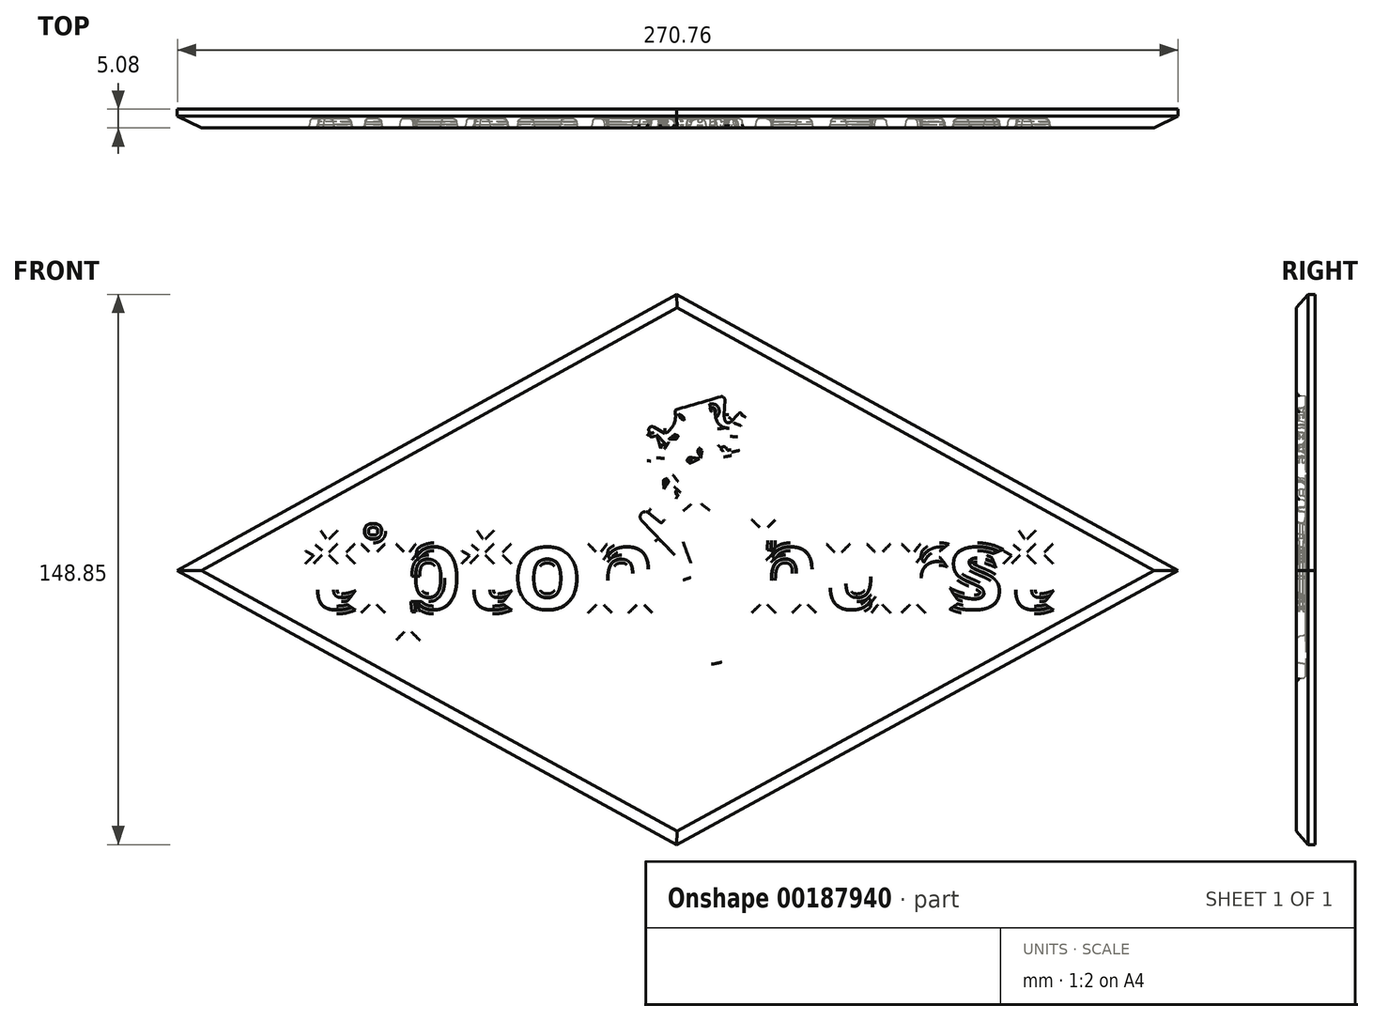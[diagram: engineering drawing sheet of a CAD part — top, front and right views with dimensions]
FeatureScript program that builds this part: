
annotation { "Feature Type Name" : "Feature", "Feature Type Description" : "" }
export const myFeature = defineFeature(function(context is Context, id is Id, definition is map)
    precondition{}
    {
        {
            var Q0;
            Q0=qCreatedBy(makeId("Front.planeOp"),FACE);
            var sketch = newSketch(context, id + "F0", { "sketchPlane" : qUnion([Q0])});
            skLineSegment(sketch, "E0", {"start": v(-28.06, 100.3) * mm, "end": v(-163.18, 25.63) * mm});
            skLineSegment(sketch, "E1", {"start": v(-163.18, 25.63) * mm, "end": v(-28.06, -48.54) * mm});
            skLineSegment(sketch, "E2", {"start": v(-28.06, -48.54) * mm, "end": v(107.58, 25.63) * mm});
            skLineSegment(sketch, "E3", {"start": v(107.58, 25.63) * mm, "end": v(-28.06, 100.3) * mm});
            skSolve(sketch);
        }
        {
            var Q0;
            Q0=makeQuery(id+"F0.imprint","IMPRINT",FACE,{"disambiguationData":[TD([[makeQuery(id+"F0.imprint","IMPRINT",EDGE,{"derivedFrom":sQuery(id+"F0.wireOp",EDGE,"E0")}),1.0]])]});
            extrude(context, id + "F1", {"entities" : qUnion([Q0]), "depth" : 5.08 * mm});
        }
        {
            var Q0;
            Q0=makeQuery(id+"F1.opExtrude","CAP_FACE",FACE,{"disambiguationData":[OSD([sQuery(id+"F0.wireOp",EDGE,"E0"),sQuery(id+"F0.wireOp",EDGE,"E1"),sQuery(id+"F0.wireOp",EDGE,"E2"),sQuery(id+"F0.wireOp",EDGE,"E3")])],"isStart":false});
            chamfer(context, id + "F2", {"entities" : qUnion([Q0]), "width" : 3.17 * mm, "tangentPropagation" : true});
        }
        {
            var Q0;
            Q0=makeQuery(id+"F1.opExtrude","CAP_FACE",FACE,{"disambiguationData":[OSD([sQuery(id+"F0.wireOp",EDGE,"E0"),sQuery(id+"F0.wireOp",EDGE,"E1"),sQuery(id+"F0.wireOp",EDGE,"E2"),sQuery(id+"F0.wireOp",EDGE,"E3")])],"isStart":false});
            var sketch = newSketch(context, id + "F3", { "sketchPlane" : qUnion([Q0])});
            skText(sketch, "E4", { "text": "tipton   hurst", "fontName": "OpenSans-Bold.ttf"});
            skLineSegment(sketch, "E5", {"start": v(-20.16, 42.62) * mm, "end": v(-20.16, 6.44) * mm});
            skLineSegment(sketch, "E6", {"start": v(-25.51, 42.4) * mm, "end": v(-25.51, 31.01) * mm});
            skLineSegment(sketch, "E7", {"start": v(-17.12, 0.55) * mm, "end": v(-19.21, -3.03) * mm});
            skArc(sketch, "E8", {"start": v(-20.16, 6.44) * mm, "mid": v(-19.36, 3.12) * mm, "end": v(-17.12, 0.55) * mm});
            skArc(sketch, "E9", {"start": v(-25.51, 6.44) * mm, "mid": v(-24.5, 1.2) * mm, "end": v(-21.64, -3.31) * mm});
            skLineSegment(sketch, "E10", {"start": v(-25.51, 23.32) * mm, "end": v(-33.26, 34.1) * mm});
            skLineSegment(sketch, "E11", {"start": v(-33.26, 34.1) * mm, "end": v(-37.86, 38.9) * mm});
            skArc(sketch, "E12", {"start": v(-35.65, 41.62) * mm, "mid": v(-37.96, 41.24) * mm, "end": v(-37.86, 38.9) * mm});
            skArc(sketch, "E13", {"start": v(-35.2, 55.27) * mm, "mid": v(-32.86, 46.95) * mm, "end": v(-25.51, 42.4) * mm});
            skLineSegment(sketch, "E14", {"start": v(-12.44, 61.8) * mm, "end": v(-11.51, 65.09) * mm});
            skLineSegment(sketch, "E15", {"start": v(-11.51, 65.09) * mm, "end": v(-10.3, 67.52) * mm});
            skLineSegment(sketch, "E16", {"start": v(-35.25, 61.69) * mm, "end": v(-35.7, 62.83) * mm});
            skLineSegment(sketch, "E17", {"start": v(-28.54, 50.71) * mm, "end": v(-23.87, 55.55) * mm});
            skLineSegment(sketch, "E18", {"start": v(-30.85, 59.33) * mm, "end": v(-23.87, 55.55) * mm});
            skLineSegment(sketch, "E19", {"start": v(-21.81, 57.7) * mm, "end": v(-28.76, 61.64) * mm});
            skLineSegment(sketch, "E20", {"start": v(-28.59, 46.65) * mm, "end": v(-15.56, 58.96) * mm});
            skPoint(sketch, "E20.startSnap0", {"position": v(-28.59, 58.1) * mm});
            skArc(sketch, "E21", {"start": v(-34.2, 64.74) * mm, "mid": v(-35.77, 64.43) * mm, "end": v(-35.7, 62.83) * mm});
            skLineSegment(sketch, "E22", {"start": v(-28.76, 61.64) * mm, "end": v(-26.7, 67.01) * mm});
            skLineSegment(sketch, "E23", {"start": v(-26.7, 67.01) * mm, "end": v(-17.18, 69.95) * mm});
            skArc(sketch, "E24", {"start": v(-17.18, 69.95) * mm, "mid": v(-17.84, 66.64) * mm, "end": v(-15.65, 64.08) * mm});
            skLineSegment(sketch, "E25", {"start": v(-14.96, 67.7) * mm, "end": v(-14.7, 71.66) * mm});
            skArc(sketch, "E26", {"start": v(-31.24, 63.05) * mm, "mid": v(-29.2, 65.33) * mm, "end": v(-28.89, 68.36) * mm});
            skArc(sketch, "E27", {"start": v(-28.16, 69.55) * mm, "mid": v(-22.24, 71.21) * mm, "end": v(-16.33, 72.95) * mm});
            skArc(sketch, "E28", {"start": v(-10.3, 67.52) * mm, "mid": v(-10.54, 68.47) * mm, "end": v(-11.51, 68.38) * mm});
            skArc(sketch, "E29", {"start": v(-32.28, 56) * mm, "mid": v(-32.34, 52.55) * mm, "end": v(-31.12, 49.34) * mm});
            skLineSegment(sketch, "E30.trimOffspring", {"start": v(-31.24, 63.05) * mm, "end": v(-34.2, 64.74) * mm});
            skPoint(sketch, "E31.orphan", {"position": v(-33.3, 60.66) * mm});
            skLineSegment(sketch, "E32.trimOffspring", {"start": v(-14.56, 65.21) * mm, "end": v(-11.51, 68.38) * mm});
            skLineSegment(sketch, "E33", {"start": v(-12.44, 61.8) * mm, "end": v(-12, 57.9) * mm});
            skLineSegment(sketch, "E34", {"start": v(-14.49, 56.49) * mm, "end": v(-14.88, 60.02) * mm});
            skLineSegment(sketch, "E35", {"start": v(-14.88, 60.02) * mm, "end": v(-15.56, 58.96) * mm});
            skPoint(sketch, "E36.orphan", {"position": v(-12.95, 60.02) * mm});
            skLineSegment(sketch, "E37", {"start": v(-35.25, 61.69) * mm, "end": v(-35.2, 55.27) * mm});
            skLineSegment(sketch, "E38", {"start": v(-32.28, 56) * mm, "end": v(-32.28, 60.2) * mm});
            skLineSegment(sketch, "E39", {"start": v(-32.28, 60.2) * mm, "end": v(-30.85, 59.33) * mm});
            skPoint(sketch, "E40.orphan", {"position": v(-34.2, 59.03) * mm});
            skPoint(sketch, "E41.visualSharp", {"position": v(-20.16, -4.66) * mm});
            skArc(sketch, "E41.filletArc", {"start": v(-21.64, -3.31) * mm, "mid": v(-20.35, -3.78) * mm, "end": v(-19.21, -3.03) * mm});
            skPoint(sketch, "E42.visualSharp", {"position": v(-29.18, 69.28) * mm});
            skArc(sketch, "E42.filletArc", {"start": v(-28.16, 69.55) * mm, "mid": v(-28.76, 69.1) * mm, "end": v(-28.89, 68.36) * mm});
            skPoint(sketch, "E43.visualSharp", {"position": v(-14.58, 73.49) * mm});
            skArc(sketch, "E43.filletArc", {"start": v(-14.7, 71.66) * mm, "mid": v(-15.18, 72.73) * mm, "end": v(-16.33, 72.95) * mm});
            skLineSegment(sketch, "E44", {"start": v(-14.56, 65.21) * mm, "end": v(-14.96, 67.7) * mm});
            skLineSegment(sketch, "E45", {"start": v(-31.12, 49.34) * mm, "end": v(-28.54, 50.71) * mm});
            skArc(sketch, "E46.trimOffspring", {"start": v(-28.59, 46.65) * mm, "mid": v(-18.09, 46.62) * mm, "end": v(-14.49, 56.49) * mm});
            skArc(sketch, "E47.trimOffspring", {"start": v(-20.16, 42.62) * mm, "mid": v(-12.8, 48.5) * mm, "end": v(-12, 57.9) * mm});
            skLineSegment(sketch, "E48.trimOffspring", {"start": v(-21.81, 57.7) * mm, "end": v(-15.65, 64.08) * mm});
            skLineSegment(sketch, "E49.trimOffspring", {"start": v(-25.51, 23.32) * mm, "end": v(-25.51, 6.44) * mm});
            skLineSegment(sketch, "E50", {"start": v(-35.65, 41.62) * mm, "end": v(-32.06, 38.65) * mm});
            skLineSegment(sketch, "E51", {"start": v(-32.06, 38.65) * mm, "end": v(-25.51, 31.01) * mm});
            const initialGuessF3  = {"E4": [-0.1283, 0.01506, 1, 0, 0.02219]};
            skSetInitialGuess(sketch, initialGuessF3);
            skSolve(sketch);
        }
        {
            var Q0;
            Q0=makeQuery(id+"F3.imprint","IMPRINT",FACE,{"disambiguationData":[TD([[makeQuery(id+"F3.imprint","IMPRINT",EDGE,{"derivedFrom":sQuery(id+"F3.wireOp",EDGE,"E4.sketch_text.stroke-50")}),-1.0]])]});
            var Q1;
            Q1=makeQuery(id+"F3.imprint","IMPRINT",FACE,{"disambiguationData":[TD([[makeQuery(id+"F3.imprint","IMPRINT",EDGE,{"derivedFrom":sQuery(id+"F3.wireOp",EDGE,"E4.sketch_text.stroke-27")}),-1.0]])]});
            var Q2;
            Q2=makeQuery(id+"F3.imprint","IMPRINT",FACE,{"disambiguationData":[TD([[makeQuery(id+"F3.imprint","IMPRINT",EDGE,{"derivedFrom":sQuery(id+"F3.wireOp",EDGE,"E4.sketch_text.stroke-23")}),-1.0]])]});
            var Q3;
            Q3=makeQuery(id+"F3.imprint","IMPRINT",FACE,{"disambiguationData":[TD([[makeQuery(id+"F3.imprint","IMPRINT",EDGE,{"derivedFrom":sQuery(id+"F3.wireOp",EDGE,"E4.sketch_text.stroke-18")}),-1.0]])]});
            var Q4;
            Q4=makeQuery(id+"F3.imprint","IMPRINT",FACE,{"disambiguationData":[TD([[makeQuery(id+"F3.imprint","IMPRINT",EDGE,{"derivedFrom":sQuery(id+"F3.wireOp",EDGE,"E4.sketch_text.stroke-0")}),-1.0]])]});
            var Q5;
            Q5=makeQuery(id+"F3.imprint","IMPRINT",FACE,{"disambiguationData":[TD([[makeQuery(id+"F3.imprint","IMPRINT",EDGE,{"derivedFrom":sQuery(id+"F3.wireOp",EDGE,"E4.sketch_text.stroke-68")}),-1.0]])]});
            var Q6;
            Q6=makeQuery(id+"F3.imprint","IMPRINT",FACE,{"disambiguationData":[TD([[makeQuery(id+"F3.imprint","IMPRINT",EDGE,{"derivedFrom":sQuery(id+"F3.wireOp",EDGE,"E4.sketch_text.stroke-86")}),-1.0]])]});
            var Q7;
            Q7=makeQuery(id+"F3.imprint","IMPRINT",FACE,{"disambiguationData":[TD([[makeQuery(id+"F3.imprint","IMPRINT",EDGE,{"derivedFrom":sQuery(id+"F3.wireOp",EDGE,"E5")}),-1.0]])]});
            var Q8;
            Q8=makeQuery(id+"F3.imprint","IMPRINT",FACE,{"disambiguationData":[TD([[makeQuery(id+"F3.imprint","IMPRINT",EDGE,{"derivedFrom":sQuery(id+"F3.wireOp",EDGE,"E4.sketch_text.stroke-103")}),-1.0]])]});
            var Q9;
            Q9=makeQuery(id+"F3.imprint","IMPRINT",FACE,{"disambiguationData":[TD([[makeQuery(id+"F3.imprint","IMPRINT",EDGE,{"derivedFrom":sQuery(id+"F3.wireOp",EDGE,"E4.sketch_text.stroke-120")}),-1.0]])]});
            var Q10;
            Q10=makeQuery(id+"F3.imprint","IMPRINT",FACE,{"disambiguationData":[TD([[makeQuery(id+"F3.imprint","IMPRINT",EDGE,{"derivedFrom":sQuery(id+"F3.wireOp",EDGE,"E4.sketch_text.stroke-137")}),-1.0]])]});
            var Q11;
            Q11=makeQuery(id+"F3.imprint","IMPRINT",FACE,{"disambiguationData":[TD([[makeQuery(id+"F3.imprint","IMPRINT",EDGE,{"derivedFrom":sQuery(id+"F3.wireOp",EDGE,"E4.sketch_text.stroke-150")}),-1.0]])]});
            var Q12;
            Q12=makeQuery(id+"F3.imprint","IMPRINT",FACE,{"disambiguationData":[TD([[makeQuery(id+"F3.imprint","IMPRINT",EDGE,{"derivedFrom":sQuery(id+"F3.wireOp",EDGE,"E4.sketch_text.stroke-176")}),-1.0]])]});
            extrude(context, id + "F4", {"entities" : qUnion([Q0, Q1, Q2, Q3, Q4, Q5, Q6, Q7, Q8, Q9, Q10, Q11, Q12]), "operationType" : NewBodyOperationType.REMOVE, "oppositeDirection" : true, "depth" : 2.54 * mm, "hasDraft" : true, "draftAngle" : 8 * degree, "draftPullDirection" : true});
        }
        {
            var Q0;
            Q0=makeQuery(id+"F4.boolean.opBoolean","COPY",FACE,{"derivedFrom":makeQuery(id+"F4.opExtrude","CAP_FACE",FACE,{"disambiguationData":[OSD([sQuery(id+"F3.wireOp",EDGE,"E4.sketch_text.stroke-0"),sQuery(id+"F3.wireOp",EDGE,"E4.sketch_text.stroke-1"),sQuery(id+"F3.wireOp",EDGE,"E4.sketch_text.stroke-2"),sQuery(id+"F3.wireOp",EDGE,"E4.sketch_text.stroke-3"),sQuery(id+"F3.wireOp",EDGE,"E4.sketch_text.stroke-4"),sQuery(id+"F3.wireOp",EDGE,"E4.sketch_text.stroke-5"),sQuery(id+"F3.wireOp",EDGE,"E4.sketch_text.stroke-6"),sQuery(id+"F3.wireOp",EDGE,"E4.sketch_text.stroke-7"),sQuery(id+"F3.wireOp",EDGE,"E4.sketch_text.stroke-8"),sQuery(id+"F3.wireOp",EDGE,"E4.sketch_text.stroke-9"),sQuery(id+"F3.wireOp",EDGE,"E4.sketch_text.stroke-10"),sQuery(id+"F3.wireOp",EDGE,"E4.sketch_text.stroke-11"),sQuery(id+"F3.wireOp",EDGE,"E4.sketch_text.stroke-12"),sQuery(id+"F3.wireOp",EDGE,"E4.sketch_text.stroke-13"),sQuery(id+"F3.wireOp",EDGE,"E4.sketch_text.stroke-14"),sQuery(id+"F3.wireOp",EDGE,"E4.sketch_text.stroke-15"),sQuery(id+"F3.wireOp",EDGE,"E4.sketch_text.stroke-16"),sQuery(id+"F3.wireOp",EDGE,"E4.sketch_text.stroke-17")])],"isStart":false})});
            var Q1;
            Q1=makeQuery(id+"F4.boolean.opBoolean","COPY",EDGE,{"derivedFrom":makeQuery(id+"F4.opExtrude","CAP_EDGE",EDGE,{"disambiguationData":[OSD([sQuery(id+"F3.wireOp",EDGE,"E4.sketch_text.stroke-6")])],"isStart":true})});
            var Q2;
            Q2=makeQuery(id+"F4.boolean.opBoolean","COPY",EDGE,{"derivedFrom":makeQuery(id+"F4.opExtrude","CAP_EDGE",EDGE,{"disambiguationData":[OSD([sQuery(id+"F3.wireOp",EDGE,"E4.sketch_text.stroke-7")])],"isStart":true})});
            var Q3;
            Q3=makeQuery(id+"F4.boolean.opBoolean","COPY",EDGE,{"derivedFrom":makeQuery(id+"F4.opExtrude","CAP_EDGE",EDGE,{"disambiguationData":[OSD([sQuery(id+"F3.wireOp",EDGE,"E4.sketch_text.stroke-8")])],"isStart":true})});
            var Q4;
            Q4=makeQuery(id+"F4.boolean.opBoolean","COPY",EDGE,{"derivedFrom":makeQuery(id+"F4.opExtrude","CAP_EDGE",EDGE,{"disambiguationData":[OSD([sQuery(id+"F3.wireOp",EDGE,"E4.sketch_text.stroke-9")])],"isStart":true})});
            var Q5;
            Q5=makeQuery(id+"F4.boolean.opBoolean","COPY",EDGE,{"derivedFrom":makeQuery(id+"F4.opExtrude","CAP_EDGE",EDGE,{"disambiguationData":[OSD([sQuery(id+"F3.wireOp",EDGE,"E4.sketch_text.stroke-10")])],"isStart":true})});
            var Q6;
            Q6=makeQuery(id+"F4.boolean.opBoolean","COPY",EDGE,{"derivedFrom":makeQuery(id+"F4.opExtrude","CAP_EDGE",EDGE,{"disambiguationData":[OSD([sQuery(id+"F3.wireOp",EDGE,"E4.sketch_text.stroke-11")])],"isStart":true})});
            var Q7;
            Q7=makeQuery(id+"F4.boolean.opBoolean","COPY",EDGE,{"derivedFrom":makeQuery(id+"F4.opExtrude","CAP_EDGE",EDGE,{"disambiguationData":[OSD([sQuery(id+"F3.wireOp",EDGE,"E4.sketch_text.stroke-12")])],"isStart":true})});
            var Q8;
            Q8=makeQuery(id+"F4.boolean.opBoolean","COPY",EDGE,{"derivedFrom":makeQuery(id+"F4.opExtrude","CAP_EDGE",EDGE,{"disambiguationData":[OSD([sQuery(id+"F3.wireOp",EDGE,"E4.sketch_text.stroke-13")])],"isStart":true})});
            var Q9;
            Q9=makeQuery(id+"F4.boolean.opBoolean","COPY",EDGE,{"derivedFrom":makeQuery(id+"F4.opExtrude","CAP_EDGE",EDGE,{"disambiguationData":[OSD([sQuery(id+"F3.wireOp",EDGE,"E4.sketch_text.stroke-14")])],"isStart":true})});
            var Q10;
            Q10=makeQuery(id+"F4.boolean.opBoolean","COPY",EDGE,{"derivedFrom":makeQuery(id+"F4.opExtrude","CAP_EDGE",EDGE,{"disambiguationData":[OSD([sQuery(id+"F3.wireOp",EDGE,"E4.sketch_text.stroke-15")])],"isStart":true})});
            var Q11;
            Q11=makeQuery(id+"F4.boolean.opBoolean","COPY",EDGE,{"derivedFrom":makeQuery(id+"F4.opExtrude","CAP_EDGE",EDGE,{"disambiguationData":[OSD([sQuery(id+"F3.wireOp",EDGE,"E4.sketch_text.stroke-1")])],"isStart":true})});
            var Q12;
            Q12=makeQuery(id+"F4.boolean.opBoolean","COPY",EDGE,{"derivedFrom":makeQuery(id+"F4.opExtrude","CAP_EDGE",EDGE,{"disambiguationData":[OSD([sQuery(id+"F3.wireOp",EDGE,"E4.sketch_text.stroke-3")])],"isStart":true})});
            var Q13;
            Q13=makeQuery(id+"F4.boolean.opBoolean","COPY",FACE,{"derivedFrom":makeQuery(id+"F4.opExtrude","CAP_FACE",FACE,{"disambiguationData":[OSD([sQuery(id+"F3.wireOp",EDGE,"E4.sketch_text.stroke-23"),sQuery(id+"F3.wireOp",EDGE,"E4.sketch_text.stroke-24"),sQuery(id+"F3.wireOp",EDGE,"E4.sketch_text.stroke-25"),sQuery(id+"F3.wireOp",EDGE,"E4.sketch_text.stroke-26")])],"isStart":false})});
            var Q14;
            Q14=makeQuery(id+"F4.boolean.opBoolean","COPY",EDGE,{"derivedFrom":makeQuery(id+"F4.opExtrude","CAP_EDGE",EDGE,{"disambiguationData":[OSD([sQuery(id+"F3.wireOp",EDGE,"E4.sketch_text.stroke-25")])],"isStart":true})});
            var Q15;
            Q15=makeQuery(id+"F4.boolean.opBoolean","COPY",EDGE,{"derivedFrom":makeQuery(id+"F4.opExtrude","CAP_EDGE",EDGE,{"disambiguationData":[OSD([sQuery(id+"F3.wireOp",EDGE,"E4.sketch_text.stroke-26")])],"isStart":true})});
            var Q16;
            Q16=makeQuery(id+"F4.boolean.opBoolean","COPY",EDGE,{"derivedFrom":makeQuery(id+"F4.opExtrude","CAP_EDGE",EDGE,{"disambiguationData":[OSD([sQuery(id+"F3.wireOp",EDGE,"E4.sketch_text.stroke-23")])],"isStart":true})});
            var Q17;
            Q17=makeQuery(id+"F4.boolean.opBoolean","COPY",EDGE,{"derivedFrom":makeQuery(id+"F4.opExtrude","CAP_EDGE",EDGE,{"disambiguationData":[OSD([sQuery(id+"F3.wireOp",EDGE,"E4.sketch_text.stroke-24")])],"isStart":true})});
            var Q18;
            Q18=makeQuery(id+"F4.boolean.opBoolean","COPY",FACE,{"derivedFrom":makeQuery(id+"F4.opExtrude","CAP_FACE",FACE,{"disambiguationData":[OSD([sQuery(id+"F3.wireOp",EDGE,"E4.sketch_text.stroke-18"),sQuery(id+"F3.wireOp",EDGE,"E4.sketch_text.stroke-19"),sQuery(id+"F3.wireOp",EDGE,"E4.sketch_text.stroke-20"),sQuery(id+"F3.wireOp",EDGE,"E4.sketch_text.stroke-21"),sQuery(id+"F3.wireOp",EDGE,"E4.sketch_text.stroke-22")])],"isStart":false})});
            var Q19;
            Q19=makeQuery(id+"F4.boolean.opBoolean","COPY",EDGE,{"derivedFrom":makeQuery(id+"F4.opExtrude","CAP_EDGE",EDGE,{"disambiguationData":[OSD([sQuery(id+"F3.wireOp",EDGE,"E4.sketch_text.stroke-22")])],"isStart":true})});
            var Q20;
            Q20=makeQuery(id+"F4.boolean.opBoolean","SPLIT",FACE,{"disambiguationData":[TD([makeQuery(id+"F4.opExtrude","SWEPT_FACE",FACE,{"disambiguationData":[OSD([sQuery(id+"F3.wireOp",EDGE,"E4.sketch_text.stroke-42")])]})])],"derivedFrom":makeQuery(id+"F1.opExtrude","CAP_FACE",FACE,{"disambiguationData":[OSD([sQuery(id+"F0.wireOp",EDGE,"E0"),sQuery(id+"F0.wireOp",EDGE,"E1"),sQuery(id+"F0.wireOp",EDGE,"E2"),sQuery(id+"F0.wireOp",EDGE,"E3")])],"isStart":false})});
            var Q21;
            Q21=makeQuery(id+"F4.boolean.opBoolean","COPY",EDGE,{"derivedFrom":makeQuery(id+"F4.opExtrude","CAP_EDGE",EDGE,{"disambiguationData":[OSD([sQuery(id+"F3.wireOp",EDGE,"E4.sketch_text.stroke-33")])],"isStart":true})});
            var Q22;
            Q22=makeQuery(id+"F4.boolean.opBoolean","COPY",EDGE,{"derivedFrom":makeQuery(id+"F4.opExtrude","CAP_EDGE",EDGE,{"disambiguationData":[OSD([sQuery(id+"F3.wireOp",EDGE,"E4.sketch_text.stroke-34")])],"isStart":true})});
            var Q23;
            Q23=makeQuery(id+"F4.boolean.opBoolean","COPY",EDGE,{"derivedFrom":makeQuery(id+"F4.opExtrude","CAP_EDGE",EDGE,{"disambiguationData":[OSD([sQuery(id+"F3.wireOp",EDGE,"E4.sketch_text.stroke-36")])],"isStart":true})});
            var Q24;
            Q24=makeQuery(id+"F4.boolean.opBoolean","COPY",EDGE,{"derivedFrom":makeQuery(id+"F4.opExtrude","CAP_EDGE",EDGE,{"disambiguationData":[OSD([sQuery(id+"F3.wireOp",EDGE,"E4.sketch_text.stroke-30")])],"isStart":true})});
            var Q25;
            Q25=makeQuery(id+"F4.boolean.opBoolean","COPY",EDGE,{"derivedFrom":makeQuery(id+"F4.opExtrude","CAP_EDGE",EDGE,{"disambiguationData":[OSD([sQuery(id+"F3.wireOp",EDGE,"E4.sketch_text.stroke-31")])],"isStart":true})});
            var Q26;
            Q26=makeQuery(id+"F4.boolean.opBoolean","COPY",EDGE,{"derivedFrom":makeQuery(id+"F4.opExtrude","CAP_EDGE",EDGE,{"disambiguationData":[OSD([sQuery(id+"F3.wireOp",EDGE,"E4.sketch_text.stroke-32")])],"isStart":true})});
            var Q27;
            Q27=makeQuery(id+"F4.boolean.opBoolean","COPY",EDGE,{"derivedFrom":makeQuery(id+"F4.opExtrude","CAP_EDGE",EDGE,{"disambiguationData":[OSD([sQuery(id+"F3.wireOp",EDGE,"E4.sketch_text.stroke-33")])],"isStart":false})});
            var Q28;
            Q28=makeQuery(id+"F4.boolean.opBoolean","COPY",EDGE,{"derivedFrom":makeQuery(id+"F4.opExtrude","CAP_EDGE",EDGE,{"disambiguationData":[OSD([sQuery(id+"F3.wireOp",EDGE,"E4.sketch_text.stroke-34")])],"isStart":false})});
            var Q29;
            Q29=makeQuery(id+"F4.boolean.opBoolean","COPY",EDGE,{"derivedFrom":makeQuery(id+"F4.opExtrude","CAP_EDGE",EDGE,{"disambiguationData":[OSD([sQuery(id+"F3.wireOp",EDGE,"E4.sketch_text.stroke-36")])],"isStart":false})});
            var Q30;
            Q30=makeQuery(id+"F4.boolean.opBoolean","COPY",EDGE,{"derivedFrom":makeQuery(id+"F4.opExtrude","CAP_EDGE",EDGE,{"disambiguationData":[OSD([sQuery(id+"F3.wireOp",EDGE,"E4.sketch_text.stroke-35")])],"isStart":false})});
            var Q31;
            Q31=makeQuery(id+"F4.boolean.opBoolean","COPY",EDGE,{"derivedFrom":makeQuery(id+"F4.opExtrude","CAP_EDGE",EDGE,{"disambiguationData":[OSD([sQuery(id+"F3.wireOp",EDGE,"E4.sketch_text.stroke-29")])],"isStart":false})});
            var Q32;
            Q32=makeQuery(id+"F4.boolean.opBoolean","COPY",EDGE,{"derivedFrom":makeQuery(id+"F4.opExtrude","CAP_EDGE",EDGE,{"disambiguationData":[OSD([sQuery(id+"F3.wireOp",EDGE,"E4.sketch_text.stroke-32")])],"isStart":false})});
            var Q33;
            Q33=makeQuery(id+"F4.boolean.opBoolean","COPY",EDGE,{"derivedFrom":makeQuery(id+"F4.opExtrude","CAP_EDGE",EDGE,{"disambiguationData":[OSD([sQuery(id+"F3.wireOp",EDGE,"E4.sketch_text.stroke-31")])],"isStart":false})});
            var Q34;
            Q34=makeQuery(id+"F4.boolean.opBoolean","COPY",EDGE,{"derivedFrom":makeQuery(id+"F4.opExtrude","CAP_EDGE",EDGE,{"disambiguationData":[OSD([sQuery(id+"F3.wireOp",EDGE,"E4.sketch_text.stroke-43")])],"isStart":false})});
            var Q35;
            Q35=makeQuery(id+"F4.boolean.opBoolean","COPY",EDGE,{"derivedFrom":makeQuery(id+"F4.opExtrude","CAP_EDGE",EDGE,{"disambiguationData":[OSD([sQuery(id+"F3.wireOp",EDGE,"E4.sketch_text.stroke-56")])],"isStart":true})});
            var Q36;
            Q36=makeQuery(id+"F4.boolean.opBoolean","COPY",EDGE,{"derivedFrom":makeQuery(id+"F4.opExtrude","CAP_EDGE",EDGE,{"disambiguationData":[OSD([sQuery(id+"F3.wireOp",EDGE,"E4.sketch_text.stroke-55")])],"isStart":true})});
            var Q37;
            Q37=makeQuery(id+"F4.boolean.opBoolean","COPY",EDGE,{"derivedFrom":makeQuery(id+"F4.opExtrude","CAP_EDGE",EDGE,{"disambiguationData":[OSD([sQuery(id+"F3.wireOp",EDGE,"E4.sketch_text.stroke-66")])],"isStart":true})});
            var Q38;
            Q38=makeQuery(id+"F4.boolean.opBoolean","COPY",EDGE,{"derivedFrom":makeQuery(id+"F4.opExtrude","CAP_EDGE",EDGE,{"disambiguationData":[OSD([sQuery(id+"F3.wireOp",EDGE,"E4.sketch_text.stroke-51")])],"isStart":true})});
            var Q39;
            Q39=makeQuery(id+"F4.boolean.opBoolean","COPY",EDGE,{"derivedFrom":makeQuery(id+"F4.opExtrude","CAP_EDGE",EDGE,{"disambiguationData":[OSD([sQuery(id+"F3.wireOp",EDGE,"E4.sketch_text.stroke-64")])],"isStart":true})});
            var Q40;
            Q40=makeQuery(id+"F4.boolean.opBoolean","COPY",EDGE,{"derivedFrom":makeQuery(id+"F4.opExtrude","CAP_EDGE",EDGE,{"disambiguationData":[OSD([sQuery(id+"F3.wireOp",EDGE,"E4.sketch_text.stroke-63")])],"isStart":true})});
            var Q41;
            Q41=makeQuery(id+"F4.boolean.opBoolean","COPY",EDGE,{"derivedFrom":makeQuery(id+"F4.opExtrude","CAP_EDGE",EDGE,{"disambiguationData":[OSD([sQuery(id+"F3.wireOp",EDGE,"E4.sketch_text.stroke-62")])],"isStart":true})});
            var Q42;
            Q42=makeQuery(id+"F4.boolean.opBoolean","COPY",EDGE,{"derivedFrom":makeQuery(id+"F4.opExtrude","CAP_EDGE",EDGE,{"disambiguationData":[OSD([sQuery(id+"F3.wireOp",EDGE,"E4.sketch_text.stroke-61")])],"isStart":true})});
            var Q43;
            Q43=makeQuery(id+"F4.boolean.opBoolean","COPY",EDGE,{"derivedFrom":makeQuery(id+"F4.opExtrude","CAP_EDGE",EDGE,{"disambiguationData":[OSD([sQuery(id+"F3.wireOp",EDGE,"E4.sketch_text.stroke-60")])],"isStart":true})});
            var Q44;
            Q44=makeQuery(id+"F4.boolean.opBoolean","COPY",EDGE,{"derivedFrom":makeQuery(id+"F4.opExtrude","CAP_EDGE",EDGE,{"disambiguationData":[OSD([sQuery(id+"F3.wireOp",EDGE,"E4.sketch_text.stroke-59")])],"isStart":true})});
            var Q45;
            Q45=makeQuery(id+"F4.boolean.opBoolean","COPY",EDGE,{"derivedFrom":makeQuery(id+"F4.opExtrude","CAP_EDGE",EDGE,{"disambiguationData":[OSD([sQuery(id+"F3.wireOp",EDGE,"E4.sketch_text.stroke-58")])],"isStart":true})});
            var Q46;
            Q46=makeQuery(id+"F4.boolean.opBoolean","COPY",EDGE,{"derivedFrom":makeQuery(id+"F4.opExtrude","CAP_EDGE",EDGE,{"disambiguationData":[OSD([sQuery(id+"F3.wireOp",EDGE,"E4.sketch_text.stroke-57")])],"isStart":true})});
            var Q47;
            Q47=makeQuery(id+"F4.boolean.opBoolean","COPY",FACE,{"derivedFrom":makeQuery(id+"F4.opExtrude","CAP_FACE",FACE,{"disambiguationData":[OSD([sQuery(id+"F3.wireOp",EDGE,"E4.sketch_text.stroke-50"),sQuery(id+"F3.wireOp",EDGE,"E4.sketch_text.stroke-51"),sQuery(id+"F3.wireOp",EDGE,"E4.sketch_text.stroke-52"),sQuery(id+"F3.wireOp",EDGE,"E4.sketch_text.stroke-53"),sQuery(id+"F3.wireOp",EDGE,"E4.sketch_text.stroke-54"),sQuery(id+"F3.wireOp",EDGE,"E4.sketch_text.stroke-55"),sQuery(id+"F3.wireOp",EDGE,"E4.sketch_text.stroke-56"),sQuery(id+"F3.wireOp",EDGE,"E4.sketch_text.stroke-57"),sQuery(id+"F3.wireOp",EDGE,"E4.sketch_text.stroke-58"),sQuery(id+"F3.wireOp",EDGE,"E4.sketch_text.stroke-59"),sQuery(id+"F3.wireOp",EDGE,"E4.sketch_text.stroke-60"),sQuery(id+"F3.wireOp",EDGE,"E4.sketch_text.stroke-61"),sQuery(id+"F3.wireOp",EDGE,"E4.sketch_text.stroke-62"),sQuery(id+"F3.wireOp",EDGE,"E4.sketch_text.stroke-63"),sQuery(id+"F3.wireOp",EDGE,"E4.sketch_text.stroke-64"),sQuery(id+"F3.wireOp",EDGE,"E4.sketch_text.stroke-65"),sQuery(id+"F3.wireOp",EDGE,"E4.sketch_text.stroke-66"),sQuery(id+"F3.wireOp",EDGE,"E4.sketch_text.stroke-67")])],"isStart":false})});
            var Q48;
            Q48=makeQuery(id+"F4.boolean.opBoolean","COPY",FACE,{"derivedFrom":makeQuery(id+"F4.opExtrude","CAP_FACE",FACE,{"disambiguationData":[OSD([sQuery(id+"F3.wireOp",EDGE,"E4.sketch_text.stroke-68"),sQuery(id+"F3.wireOp",EDGE,"E4.sketch_text.stroke-69"),sQuery(id+"F3.wireOp",EDGE,"E4.sketch_text.stroke-70"),sQuery(id+"F3.wireOp",EDGE,"E4.sketch_text.stroke-71"),sQuery(id+"F3.wireOp",EDGE,"E4.sketch_text.stroke-72"),sQuery(id+"F3.wireOp",EDGE,"E4.sketch_text.stroke-73"),sQuery(id+"F3.wireOp",EDGE,"E4.sketch_text.stroke-74"),sQuery(id+"F3.wireOp",EDGE,"E4.sketch_text.stroke-75"),sQuery(id+"F3.wireOp",EDGE,"E4.sketch_text.stroke-76"),sQuery(id+"F3.wireOp",EDGE,"E4.sketch_text.stroke-77"),sQuery(id+"F3.wireOp",EDGE,"E4.sketch_text.stroke-78"),sQuery(id+"F3.wireOp",EDGE,"E4.sketch_text.stroke-79"),sQuery(id+"F3.wireOp",EDGE,"E4.sketch_text.stroke-80"),sQuery(id+"F3.wireOp",EDGE,"E4.sketch_text.stroke-81"),sQuery(id+"F3.wireOp",EDGE,"E4.sketch_text.stroke-82"),sQuery(id+"F3.wireOp",EDGE,"E4.sketch_text.stroke-83"),sQuery(id+"F3.wireOp",EDGE,"E4.sketch_text.stroke-84"),sQuery(id+"F3.wireOp",EDGE,"E4.sketch_text.stroke-85")])],"isStart":false})});
            var Q49;
            Q49=makeQuery(id+"F4.boolean.opBoolean","COPY",EDGE,{"derivedFrom":makeQuery(id+"F4.opExtrude","CAP_EDGE",EDGE,{"disambiguationData":[OSD([sQuery(id+"F3.wireOp",EDGE,"E4.sketch_text.stroke-78")])],"isStart":true})});
            var Q50;
            Q50=makeQuery(id+"F4.boolean.opBoolean","COPY",EDGE,{"derivedFrom":makeQuery(id+"F4.opExtrude","CAP_EDGE",EDGE,{"disambiguationData":[OSD([sQuery(id+"F3.wireOp",EDGE,"E4.sketch_text.stroke-74")])],"isStart":true})});
            var Q51;
            Q51=makeQuery(id+"F4.boolean.opBoolean","COPY",FACE,{"derivedFrom":makeQuery(id+"F4.opExtrude","CAP_FACE",FACE,{"disambiguationData":[OSD([sQuery(id+"F3.wireOp",EDGE,"E4.sketch_text.stroke-86"),sQuery(id+"F3.wireOp",EDGE,"E4.sketch_text.stroke-87"),sQuery(id+"F3.wireOp",EDGE,"E4.sketch_text.stroke-88"),sQuery(id+"F3.wireOp",EDGE,"E4.sketch_text.stroke-89"),sQuery(id+"F3.wireOp",EDGE,"E4.sketch_text.stroke-90"),sQuery(id+"F3.wireOp",EDGE,"E4.sketch_text.stroke-91"),sQuery(id+"F3.wireOp",EDGE,"E4.sketch_text.stroke-92"),sQuery(id+"F3.wireOp",EDGE,"E4.sketch_text.stroke-93"),sQuery(id+"F3.wireOp",EDGE,"E4.sketch_text.stroke-94"),sQuery(id+"F3.wireOp",EDGE,"E4.sketch_text.stroke-95"),sQuery(id+"F3.wireOp",EDGE,"E4.sketch_text.stroke-96"),sQuery(id+"F3.wireOp",EDGE,"E4.sketch_text.stroke-97"),sQuery(id+"F3.wireOp",EDGE,"E4.sketch_text.stroke-98"),sQuery(id+"F3.wireOp",EDGE,"E4.sketch_text.stroke-99"),sQuery(id+"F3.wireOp",EDGE,"E4.sketch_text.stroke-100"),sQuery(id+"F3.wireOp",EDGE,"E4.sketch_text.stroke-101"),sQuery(id+"F3.wireOp",EDGE,"E4.sketch_text.stroke-102")])],"isStart":false})});
            var Q52;
            Q52=makeQuery(id+"F4.boolean.opBoolean","COPY",EDGE,{"derivedFrom":makeQuery(id+"F4.opExtrude","CAP_EDGE",EDGE,{"disambiguationData":[OSD([sQuery(id+"F3.wireOp",EDGE,"E4.sketch_text.stroke-89")])],"isStart":true})});
            var Q53;
            Q53=makeQuery(id+"F4.boolean.opBoolean","COPY",EDGE,{"derivedFrom":makeQuery(id+"F4.opExtrude","CAP_EDGE",EDGE,{"disambiguationData":[OSD([sQuery(id+"F3.wireOp",EDGE,"E4.sketch_text.stroke-86")])],"isStart":true})});
            var Q54;
            Q54=makeQuery(id+"F4.boolean.opBoolean","COPY",EDGE,{"derivedFrom":makeQuery(id+"F4.opExtrude","CAP_EDGE",EDGE,{"disambiguationData":[OSD([sQuery(id+"F3.wireOp",EDGE,"E4.sketch_text.stroke-102")])],"isStart":true})});
            var Q55;
            Q55=makeQuery(id+"F4.boolean.opBoolean","COPY",EDGE,{"derivedFrom":makeQuery(id+"F4.opExtrude","CAP_EDGE",EDGE,{"disambiguationData":[OSD([sQuery(id+"F3.wireOp",EDGE,"E4.sketch_text.stroke-93")])],"isStart":true})});
            var Q56;
            Q56=makeQuery(id+"F4.boolean.opBoolean","COPY",EDGE,{"derivedFrom":makeQuery(id+"F4.opExtrude","CAP_EDGE",EDGE,{"disambiguationData":[OSD([sQuery(id+"F3.wireOp",EDGE,"E4.sketch_text.stroke-94")])],"isStart":true})});
            var Q57;
            Q57=makeQuery(id+"F4.boolean.opBoolean","COPY",EDGE,{"derivedFrom":makeQuery(id+"F4.opExtrude","CAP_EDGE",EDGE,{"disambiguationData":[OSD([sQuery(id+"F3.wireOp",EDGE,"E4.sketch_text.stroke-95")])],"isStart":true})});
            var Q58;
            Q58=makeQuery(id+"F4.boolean.opBoolean","COPY",EDGE,{"derivedFrom":makeQuery(id+"F4.opExtrude","CAP_EDGE",EDGE,{"disambiguationData":[OSD([sQuery(id+"F3.wireOp",EDGE,"E4.sketch_text.stroke-96")])],"isStart":true})});
            var Q59;
            Q59=makeQuery(id+"F4.boolean.opBoolean","COPY",FACE,{"derivedFrom":makeQuery(id+"F4.opExtrude","CAP_FACE",FACE,{"disambiguationData":[OSD([sQuery(id+"F3.wireOp",EDGE,"E4.sketch_text.stroke-103"),sQuery(id+"F3.wireOp",EDGE,"E4.sketch_text.stroke-104"),sQuery(id+"F3.wireOp",EDGE,"E4.sketch_text.stroke-105"),sQuery(id+"F3.wireOp",EDGE,"E4.sketch_text.stroke-106"),sQuery(id+"F3.wireOp",EDGE,"E4.sketch_text.stroke-107"),sQuery(id+"F3.wireOp",EDGE,"E4.sketch_text.stroke-108"),sQuery(id+"F3.wireOp",EDGE,"E4.sketch_text.stroke-109"),sQuery(id+"F3.wireOp",EDGE,"E4.sketch_text.stroke-110"),sQuery(id+"F3.wireOp",EDGE,"E4.sketch_text.stroke-111"),sQuery(id+"F3.wireOp",EDGE,"E4.sketch_text.stroke-112"),sQuery(id+"F3.wireOp",EDGE,"E4.sketch_text.stroke-113"),sQuery(id+"F3.wireOp",EDGE,"E4.sketch_text.stroke-114"),sQuery(id+"F3.wireOp",EDGE,"E4.sketch_text.stroke-115"),sQuery(id+"F3.wireOp",EDGE,"E4.sketch_text.stroke-116"),sQuery(id+"F3.wireOp",EDGE,"E4.sketch_text.stroke-117"),sQuery(id+"F3.wireOp",EDGE,"E4.sketch_text.stroke-118"),sQuery(id+"F3.wireOp",EDGE,"E4.sketch_text.stroke-119")])],"isStart":false})});
            var Q60;
            Q60=makeQuery(id+"F4.boolean.opBoolean","COPY",EDGE,{"derivedFrom":makeQuery(id+"F4.opExtrude","CAP_EDGE",EDGE,{"disambiguationData":[OSD([sQuery(id+"F3.wireOp",EDGE,"E4.sketch_text.stroke-109")])],"isStart":true})});
            var Q61;
            Q61=makeQuery(id+"F4.boolean.opBoolean","COPY",EDGE,{"derivedFrom":makeQuery(id+"F4.opExtrude","CAP_EDGE",EDGE,{"disambiguationData":[OSD([sQuery(id+"F3.wireOp",EDGE,"E4.sketch_text.stroke-108")])],"isStart":true})});
            var Q62;
            Q62=makeQuery(id+"F4.boolean.opBoolean","COPY",EDGE,{"derivedFrom":makeQuery(id+"F4.opExtrude","CAP_EDGE",EDGE,{"disambiguationData":[OSD([sQuery(id+"F3.wireOp",EDGE,"E4.sketch_text.stroke-103")])],"isStart":true})});
            var Q63;
            Q63=makeQuery(id+"F4.boolean.opBoolean","COPY",EDGE,{"derivedFrom":makeQuery(id+"F4.opExtrude","CAP_EDGE",EDGE,{"disambiguationData":[OSD([sQuery(id+"F3.wireOp",EDGE,"E4.sketch_text.stroke-119")])],"isStart":true})});
            var Q64;
            Q64=makeQuery(id+"F4.boolean.opBoolean","COPY",EDGE,{"derivedFrom":makeQuery(id+"F4.opExtrude","CAP_EDGE",EDGE,{"disambiguationData":[OSD([sQuery(id+"F3.wireOp",EDGE,"E4.sketch_text.stroke-110")])],"isStart":true})});
            var Q65;
            Q65=makeQuery(id+"F4.boolean.opBoolean","COPY",EDGE,{"derivedFrom":makeQuery(id+"F4.opExtrude","CAP_EDGE",EDGE,{"disambiguationData":[OSD([sQuery(id+"F3.wireOp",EDGE,"E4.sketch_text.stroke-111")])],"isStart":true})});
            var Q66;
            Q66=makeQuery(id+"F4.boolean.opBoolean","COPY",EDGE,{"derivedFrom":makeQuery(id+"F4.opExtrude","CAP_EDGE",EDGE,{"disambiguationData":[OSD([sQuery(id+"F3.wireOp",EDGE,"E4.sketch_text.stroke-112")])],"isStart":true})});
            var Q67;
            Q67=makeQuery(id+"F4.boolean.opBoolean","COPY",EDGE,{"derivedFrom":makeQuery(id+"F4.opExtrude","CAP_EDGE",EDGE,{"disambiguationData":[OSD([sQuery(id+"F3.wireOp",EDGE,"E4.sketch_text.stroke-124")])],"isStart":true})});
            var Q68;
            Q68=makeQuery(id+"F4.boolean.opBoolean","COPY",EDGE,{"derivedFrom":makeQuery(id+"F4.opExtrude","CAP_EDGE",EDGE,{"disambiguationData":[OSD([sQuery(id+"F3.wireOp",EDGE,"E4.sketch_text.stroke-136")])],"isStart":true})});
            var Q69;
            Q69=makeQuery(id+"F4.boolean.opBoolean","COPY",EDGE,{"derivedFrom":makeQuery(id+"F4.opExtrude","CAP_EDGE",EDGE,{"disambiguationData":[OSD([sQuery(id+"F3.wireOp",EDGE,"E4.sketch_text.stroke-120")])],"isStart":true})});
            var Q70;
            Q70=makeQuery(id+"F4.boolean.opBoolean","COPY",EDGE,{"derivedFrom":makeQuery(id+"F4.opExtrude","CAP_EDGE",EDGE,{"disambiguationData":[OSD([sQuery(id+"F3.wireOp",EDGE,"E4.sketch_text.stroke-135")])],"isStart":true})});
            var Q71;
            Q71=makeQuery(id+"F4.boolean.opBoolean","COPY",EDGE,{"derivedFrom":makeQuery(id+"F4.opExtrude","CAP_EDGE",EDGE,{"disambiguationData":[OSD([sQuery(id+"F3.wireOp",EDGE,"E4.sketch_text.stroke-133")])],"isStart":true})});
            var Q72;
            Q72=makeQuery(id+"F4.boolean.opBoolean","COPY",EDGE,{"derivedFrom":makeQuery(id+"F4.opExtrude","CAP_EDGE",EDGE,{"disambiguationData":[OSD([sQuery(id+"F3.wireOp",EDGE,"E4.sketch_text.stroke-127")])],"isStart":true})});
            var Q73;
            Q73=makeQuery(id+"F4.boolean.opBoolean","COPY",EDGE,{"derivedFrom":makeQuery(id+"F4.opExtrude","CAP_EDGE",EDGE,{"disambiguationData":[OSD([sQuery(id+"F3.wireOp",EDGE,"E4.sketch_text.stroke-134")])],"isStart":true})});
            var Q74;
            Q74=makeQuery(id+"F4.boolean.opBoolean","COPY",FACE,{"derivedFrom":makeQuery(id+"F4.opExtrude","CAP_FACE",FACE,{"disambiguationData":[OSD([sQuery(id+"F3.wireOp",EDGE,"E4.sketch_text.stroke-120"),sQuery(id+"F3.wireOp",EDGE,"E4.sketch_text.stroke-121"),sQuery(id+"F3.wireOp",EDGE,"E4.sketch_text.stroke-122"),sQuery(id+"F3.wireOp",EDGE,"E4.sketch_text.stroke-123"),sQuery(id+"F3.wireOp",EDGE,"E4.sketch_text.stroke-124"),sQuery(id+"F3.wireOp",EDGE,"E4.sketch_text.stroke-125"),sQuery(id+"F3.wireOp",EDGE,"E4.sketch_text.stroke-126"),sQuery(id+"F3.wireOp",EDGE,"E4.sketch_text.stroke-127"),sQuery(id+"F3.wireOp",EDGE,"E4.sketch_text.stroke-128"),sQuery(id+"F3.wireOp",EDGE,"E4.sketch_text.stroke-129"),sQuery(id+"F3.wireOp",EDGE,"E4.sketch_text.stroke-130"),sQuery(id+"F3.wireOp",EDGE,"E4.sketch_text.stroke-131"),sQuery(id+"F3.wireOp",EDGE,"E4.sketch_text.stroke-132"),sQuery(id+"F3.wireOp",EDGE,"E4.sketch_text.stroke-133"),sQuery(id+"F3.wireOp",EDGE,"E4.sketch_text.stroke-134"),sQuery(id+"F3.wireOp",EDGE,"E4.sketch_text.stroke-135"),sQuery(id+"F3.wireOp",EDGE,"E4.sketch_text.stroke-136")])],"isStart":false})});
            var Q75;
            Q75=makeQuery(id+"F4.boolean.opBoolean","COPY",FACE,{"derivedFrom":makeQuery(id+"F4.opExtrude","CAP_FACE",FACE,{"disambiguationData":[OSD([sQuery(id+"F3.wireOp",EDGE,"E4.sketch_text.stroke-137"),sQuery(id+"F3.wireOp",EDGE,"E4.sketch_text.stroke-138"),sQuery(id+"F3.wireOp",EDGE,"E4.sketch_text.stroke-139"),sQuery(id+"F3.wireOp",EDGE,"E4.sketch_text.stroke-140"),sQuery(id+"F3.wireOp",EDGE,"E4.sketch_text.stroke-141"),sQuery(id+"F3.wireOp",EDGE,"E4.sketch_text.stroke-142"),sQuery(id+"F3.wireOp",EDGE,"E4.sketch_text.stroke-143"),sQuery(id+"F3.wireOp",EDGE,"E4.sketch_text.stroke-144"),sQuery(id+"F3.wireOp",EDGE,"E4.sketch_text.stroke-145"),sQuery(id+"F3.wireOp",EDGE,"E4.sketch_text.stroke-146"),sQuery(id+"F3.wireOp",EDGE,"E4.sketch_text.stroke-147"),sQuery(id+"F3.wireOp",EDGE,"E4.sketch_text.stroke-148"),sQuery(id+"F3.wireOp",EDGE,"E4.sketch_text.stroke-149")])],"isStart":false})});
            var Q76;
            Q76=makeQuery(id+"F4.boolean.opBoolean","COPY",EDGE,{"derivedFrom":makeQuery(id+"F4.opExtrude","CAP_EDGE",EDGE,{"disambiguationData":[OSD([sQuery(id+"F3.wireOp",EDGE,"E4.sketch_text.stroke-142")])],"isStart":true})});
            var Q77;
            Q77=makeQuery(id+"F4.boolean.opBoolean","COPY",EDGE,{"derivedFrom":makeQuery(id+"F4.opExtrude","CAP_EDGE",EDGE,{"disambiguationData":[OSD([sQuery(id+"F3.wireOp",EDGE,"E4.sketch_text.stroke-138")])],"isStart":true})});
            var Q78;
            Q78=makeQuery(id+"F4.boolean.opBoolean","COPY",EDGE,{"derivedFrom":makeQuery(id+"F4.opExtrude","CAP_EDGE",EDGE,{"disambiguationData":[OSD([sQuery(id+"F3.wireOp",EDGE,"E4.sketch_text.stroke-143")])],"isStart":true})});
            var Q79;
            Q79=makeQuery(id+"F4.boolean.opBoolean","COPY",EDGE,{"derivedFrom":makeQuery(id+"F4.opExtrude","CAP_EDGE",EDGE,{"disambiguationData":[OSD([sQuery(id+"F3.wireOp",EDGE,"E4.sketch_text.stroke-144")])],"isStart":true})});
            var Q80;
            Q80=makeQuery(id+"F4.boolean.opBoolean","COPY",EDGE,{"derivedFrom":makeQuery(id+"F4.opExtrude","CAP_EDGE",EDGE,{"disambiguationData":[OSD([sQuery(id+"F3.wireOp",EDGE,"E4.sketch_text.stroke-145")])],"isStart":true})});
            var Q81;
            Q81=makeQuery(id+"F4.boolean.opBoolean","COPY",EDGE,{"derivedFrom":makeQuery(id+"F4.opExtrude","CAP_EDGE",EDGE,{"disambiguationData":[OSD([sQuery(id+"F3.wireOp",EDGE,"E4.sketch_text.stroke-146")])],"isStart":true})});
            var Q82;
            Q82=makeQuery(id+"F4.boolean.opBoolean","COPY",EDGE,{"derivedFrom":makeQuery(id+"F4.opExtrude","CAP_EDGE",EDGE,{"disambiguationData":[OSD([sQuery(id+"F3.wireOp",EDGE,"E4.sketch_text.stroke-149")])],"isStart":true})});
            var Q83;
            Q83=makeQuery(id+"F4.boolean.opBoolean","COPY",FACE,{"derivedFrom":makeQuery(id+"F4.opExtrude","CAP_FACE",FACE,{"disambiguationData":[OSD([sQuery(id+"F3.wireOp",EDGE,"E4.sketch_text.stroke-150"),sQuery(id+"F3.wireOp",EDGE,"E4.sketch_text.stroke-151"),sQuery(id+"F3.wireOp",EDGE,"E4.sketch_text.stroke-152"),sQuery(id+"F3.wireOp",EDGE,"E4.sketch_text.stroke-153"),sQuery(id+"F3.wireOp",EDGE,"E4.sketch_text.stroke-154"),sQuery(id+"F3.wireOp",EDGE,"E4.sketch_text.stroke-155"),sQuery(id+"F3.wireOp",EDGE,"E4.sketch_text.stroke-156"),sQuery(id+"F3.wireOp",EDGE,"E4.sketch_text.stroke-157"),sQuery(id+"F3.wireOp",EDGE,"E4.sketch_text.stroke-158"),sQuery(id+"F3.wireOp",EDGE,"E4.sketch_text.stroke-159"),sQuery(id+"F3.wireOp",EDGE,"E4.sketch_text.stroke-160"),sQuery(id+"F3.wireOp",EDGE,"E4.sketch_text.stroke-161"),sQuery(id+"F3.wireOp",EDGE,"E4.sketch_text.stroke-162"),sQuery(id+"F3.wireOp",EDGE,"E4.sketch_text.stroke-163"),sQuery(id+"F3.wireOp",EDGE,"E4.sketch_text.stroke-164"),sQuery(id+"F3.wireOp",EDGE,"E4.sketch_text.stroke-165"),sQuery(id+"F3.wireOp",EDGE,"E4.sketch_text.stroke-166"),sQuery(id+"F3.wireOp",EDGE,"E4.sketch_text.stroke-167"),sQuery(id+"F3.wireOp",EDGE,"E4.sketch_text.stroke-168"),sQuery(id+"F3.wireOp",EDGE,"E4.sketch_text.stroke-169"),sQuery(id+"F3.wireOp",EDGE,"E4.sketch_text.stroke-170"),sQuery(id+"F3.wireOp",EDGE,"E4.sketch_text.stroke-171"),sQuery(id+"F3.wireOp",EDGE,"E4.sketch_text.stroke-172"),sQuery(id+"F3.wireOp",EDGE,"E4.sketch_text.stroke-173"),sQuery(id+"F3.wireOp",EDGE,"E4.sketch_text.stroke-174"),sQuery(id+"F3.wireOp",EDGE,"E4.sketch_text.stroke-175")])],"isStart":false})});
            var Q84;
            Q84=makeQuery(id+"F4.boolean.opBoolean","COPY",EDGE,{"derivedFrom":makeQuery(id+"F4.opExtrude","CAP_EDGE",EDGE,{"disambiguationData":[OSD([sQuery(id+"F3.wireOp",EDGE,"E4.sketch_text.stroke-167")])],"isStart":true})});
            var Q85;
            Q85=makeQuery(id+"F4.boolean.opBoolean","COPY",EDGE,{"derivedFrom":makeQuery(id+"F4.opExtrude","CAP_EDGE",EDGE,{"disambiguationData":[OSD([sQuery(id+"F3.wireOp",EDGE,"E4.sketch_text.stroke-154")])],"isStart":true})});
            var Q86;
            Q86=makeQuery(id+"F4.boolean.opBoolean","COPY",EDGE,{"derivedFrom":makeQuery(id+"F4.opExtrude","CAP_EDGE",EDGE,{"disambiguationData":[OSD([sQuery(id+"F3.wireOp",EDGE,"E4.sketch_text.stroke-161")])],"isStart":true})});
            var Q87;
            Q87=makeQuery(id+"F4.boolean.opBoolean","COPY",EDGE,{"derivedFrom":makeQuery(id+"F4.opExtrude","CAP_EDGE",EDGE,{"disambiguationData":[OSD([sQuery(id+"F3.wireOp",EDGE,"E4.sketch_text.stroke-151")])],"isStart":true})});
            var Q88;
            Q88=makeQuery(id+"F4.boolean.opBoolean","COPY",EDGE,{"derivedFrom":makeQuery(id+"F4.opExtrude","CAP_EDGE",EDGE,{"disambiguationData":[OSD([sQuery(id+"F3.wireOp",EDGE,"E4.sketch_text.stroke-168")])],"isStart":true})});
            var Q89;
            Q89=makeQuery(id+"F4.boolean.opBoolean","COPY",FACE,{"derivedFrom":makeQuery(id+"F4.opExtrude","CAP_FACE",FACE,{"disambiguationData":[OSD([sQuery(id+"F3.wireOp",EDGE,"E4.sketch_text.stroke-176"),sQuery(id+"F3.wireOp",EDGE,"E4.sketch_text.stroke-177"),sQuery(id+"F3.wireOp",EDGE,"E4.sketch_text.stroke-178"),sQuery(id+"F3.wireOp",EDGE,"E4.sketch_text.stroke-179"),sQuery(id+"F3.wireOp",EDGE,"E4.sketch_text.stroke-180"),sQuery(id+"F3.wireOp",EDGE,"E4.sketch_text.stroke-181"),sQuery(id+"F3.wireOp",EDGE,"E4.sketch_text.stroke-182"),sQuery(id+"F3.wireOp",EDGE,"E4.sketch_text.stroke-183"),sQuery(id+"F3.wireOp",EDGE,"E4.sketch_text.stroke-184"),sQuery(id+"F3.wireOp",EDGE,"E4.sketch_text.stroke-185"),sQuery(id+"F3.wireOp",EDGE,"E4.sketch_text.stroke-186"),sQuery(id+"F3.wireOp",EDGE,"E4.sketch_text.stroke-187"),sQuery(id+"F3.wireOp",EDGE,"E4.sketch_text.stroke-188"),sQuery(id+"F3.wireOp",EDGE,"E4.sketch_text.stroke-189"),sQuery(id+"F3.wireOp",EDGE,"E4.sketch_text.stroke-190"),sQuery(id+"F3.wireOp",EDGE,"E4.sketch_text.stroke-191"),sQuery(id+"F3.wireOp",EDGE,"E4.sketch_text.stroke-192"),sQuery(id+"F3.wireOp",EDGE,"E4.sketch_text.stroke-193")])],"isStart":false})});
            var Q90;
            Q90=makeQuery(id+"F4.boolean.opBoolean","COPY",EDGE,{"derivedFrom":makeQuery(id+"F4.opExtrude","CAP_EDGE",EDGE,{"disambiguationData":[OSD([sQuery(id+"F3.wireOp",EDGE,"E4.sketch_text.stroke-181")])],"isStart":true})});
            var Q91;
            Q91=makeQuery(id+"F4.boolean.opBoolean","COPY",EDGE,{"derivedFrom":makeQuery(id+"F4.opExtrude","CAP_EDGE",EDGE,{"disambiguationData":[OSD([sQuery(id+"F3.wireOp",EDGE,"E4.sketch_text.stroke-182")])],"isStart":true})});
            var Q92;
            Q92=makeQuery(id+"F4.boolean.opBoolean","COPY",EDGE,{"derivedFrom":makeQuery(id+"F4.opExtrude","CAP_EDGE",EDGE,{"disambiguationData":[OSD([sQuery(id+"F3.wireOp",EDGE,"E4.sketch_text.stroke-183")])],"isStart":true})});
            var Q93;
            Q93=makeQuery(id+"F4.boolean.opBoolean","COPY",EDGE,{"derivedFrom":makeQuery(id+"F4.opExtrude","CAP_EDGE",EDGE,{"disambiguationData":[OSD([sQuery(id+"F3.wireOp",EDGE,"E4.sketch_text.stroke-184")])],"isStart":true})});
            var Q94;
            Q94=makeQuery(id+"F4.boolean.opBoolean","COPY",EDGE,{"derivedFrom":makeQuery(id+"F4.opExtrude","CAP_EDGE",EDGE,{"disambiguationData":[OSD([sQuery(id+"F3.wireOp",EDGE,"E4.sketch_text.stroke-185")])],"isStart":true})});
            var Q95;
            Q95=makeQuery(id+"F4.boolean.opBoolean","COPY",EDGE,{"derivedFrom":makeQuery(id+"F4.opExtrude","CAP_EDGE",EDGE,{"disambiguationData":[OSD([sQuery(id+"F3.wireOp",EDGE,"E4.sketch_text.stroke-186")])],"isStart":true})});
            var Q96;
            Q96=makeQuery(id+"F4.boolean.opBoolean","COPY",EDGE,{"derivedFrom":makeQuery(id+"F4.opExtrude","CAP_EDGE",EDGE,{"disambiguationData":[OSD([sQuery(id+"F3.wireOp",EDGE,"E4.sketch_text.stroke-187")])],"isStart":true})});
            var Q97;
            Q97=makeQuery(id+"F4.boolean.opBoolean","COPY",EDGE,{"derivedFrom":makeQuery(id+"F4.opExtrude","CAP_EDGE",EDGE,{"disambiguationData":[OSD([sQuery(id+"F3.wireOp",EDGE,"E4.sketch_text.stroke-188")])],"isStart":true})});
            var Q98;
            Q98=makeQuery(id+"F4.boolean.opBoolean","COPY",EDGE,{"derivedFrom":makeQuery(id+"F4.opExtrude","CAP_EDGE",EDGE,{"disambiguationData":[OSD([sQuery(id+"F3.wireOp",EDGE,"E4.sketch_text.stroke-189")])],"isStart":true})});
            var Q99;
            Q99=makeQuery(id+"F4.boolean.opBoolean","COPY",EDGE,{"derivedFrom":makeQuery(id+"F4.opExtrude","CAP_EDGE",EDGE,{"disambiguationData":[OSD([sQuery(id+"F3.wireOp",EDGE,"E4.sketch_text.stroke-190")])],"isStart":true})});
            var Q100;
            Q100=makeQuery(id+"F4.boolean.opBoolean","COPY",EDGE,{"derivedFrom":makeQuery(id+"F4.opExtrude","CAP_EDGE",EDGE,{"disambiguationData":[OSD([sQuery(id+"F3.wireOp",EDGE,"E4.sketch_text.stroke-191")])],"isStart":true})});
            var Q101;
            Q101=makeQuery(id+"F4.boolean.opBoolean","COPY",EDGE,{"derivedFrom":makeQuery(id+"F4.opExtrude","CAP_EDGE",EDGE,{"disambiguationData":[OSD([sQuery(id+"F3.wireOp",EDGE,"E4.sketch_text.stroke-177")])],"isStart":true})});
            fillet(context, id + "F5", {"entities" : qUnion([Q0, Q1, Q2, Q3, Q4, Q5, Q6, Q7, Q8, Q9, Q10, Q11, Q12, Q13, Q14, Q15, Q16, Q17, Q18, Q19, Q20, Q21, Q22, Q23, Q24, Q25, Q26, Q27, Q28, Q29, Q30, Q31, Q32, Q33, Q34, Q35, Q36, Q37, Q38, Q39, Q40, Q41, Q42, Q43, Q44, Q45, Q46, Q47, Q48, Q49, Q50, Q51, Q52, Q53, Q54, Q55, Q56, Q57, Q58, Q59, Q60, Q61, Q62, Q63, Q64, Q65, Q66, Q67, Q68, Q69, Q70, Q71, Q72, Q73, Q74, Q75, Q76, Q77, Q78, Q79, Q80, Q81, Q82, Q83, Q84, Q85, Q86, Q87, Q88, Q89, Q90, Q91, Q92, Q93, Q94, Q95, Q96, Q97, Q98, Q99, Q100, Q101]), "radius" : 1.02 * mm, "tangentPropagation" : true, "allowEdgeOverflow" : false});
        }
        {
            var Q0;
            Q0=makeQuery(id+"F4.boolean.opBoolean","COPY",EDGE,{"derivedFrom":makeQuery(id+"F4.opExtrude","CAP_EDGE",EDGE,{"disambiguationData":[OSD([sQuery(id+"F3.wireOp",EDGE,"E10")])],"isStart":false})});
            var Q1;
            Q1=makeQuery(id+"F4.boolean.opBoolean","COPY",EDGE,{"derivedFrom":makeQuery(id+"F4.opExtrude","CAP_EDGE",EDGE,{"disambiguationData":[OSD([sQuery(id+"F3.wireOp",EDGE,"E6")])],"isStart":false})});
            var Q2;
            Q2=makeQuery(id+"F4.boolean.opBoolean","COPY",EDGE,{"derivedFrom":makeQuery(id+"F4.opExtrude","CAP_EDGE",EDGE,{"disambiguationData":[OSD([sQuery(id+"F3.wireOp",EDGE,"E5")])],"isStart":false})});
            var Q3;
            Q3=makeQuery(id+"F4.boolean.opBoolean","COPY",EDGE,{"derivedFrom":makeQuery(id+"F4.opExtrude","CAP_EDGE",EDGE,{"disambiguationData":[OSD([sQuery(id+"F3.wireOp",EDGE,"E51")])],"isStart":false})});
            var Q4;
            Q4=makeQuery(id+"F4.boolean.opBoolean","COPY",EDGE,{"derivedFrom":makeQuery(id+"F4.opExtrude","CAP_EDGE",EDGE,{"disambiguationData":[OSD([sQuery(id+"F3.wireOp",EDGE,"E10")])],"isStart":true})});
            var Q5;
            Q5=makeQuery(id+"F4.boolean.opBoolean","COPY",EDGE,{"derivedFrom":makeQuery(id+"F4.opExtrude","CAP_EDGE",EDGE,{"disambiguationData":[OSD([sQuery(id+"F3.wireOp",EDGE,"E51")])],"isStart":true})});
            var Q6;
            Q6=makeQuery(id+"F4.boolean.opBoolean","COPY",EDGE,{"derivedFrom":makeQuery(id+"F4.opExtrude","CAP_EDGE",EDGE,{"disambiguationData":[OSD([sQuery(id+"F3.wireOp",EDGE,"E6")])],"isStart":true})});
            var Q7;
            Q7=makeQuery(id+"F4.boolean.opBoolean","COPY",EDGE,{"derivedFrom":makeQuery(id+"F4.opExtrude","CAP_EDGE",EDGE,{"disambiguationData":[OSD([sQuery(id+"F3.wireOp",EDGE,"E49.trimOffspring")])],"isStart":true})});
            var Q8;
            Q8=makeQuery(id+"F4.boolean.opBoolean","COPY",EDGE,{"derivedFrom":makeQuery(id+"F4.opExtrude","CAP_EDGE",EDGE,{"disambiguationData":[OSD([sQuery(id+"F3.wireOp",EDGE,"E9")])],"isStart":false})});
            var Q9;
            Q9=makeQuery(id+"F4.boolean.opBoolean","COPY",EDGE,{"derivedFrom":makeQuery(id+"F4.opExtrude","CAP_EDGE",EDGE,{"disambiguationData":[OSD([sQuery(id+"F3.wireOp",EDGE,"E8")])],"isStart":true})});
            var Q10;
            Q10=makeQuery(id+"F4.boolean.opBoolean","COPY",EDGE,{"derivedFrom":makeQuery(id+"F4.opExtrude","CAP_EDGE",EDGE,{"disambiguationData":[OSD([sQuery(id+"F3.wireOp",EDGE,"E12")])],"isStart":true})});
            var Q11;
            Q11=makeQuery(id+"F4.boolean.opBoolean","COPY",EDGE,{"derivedFrom":makeQuery(id+"F4.opExtrude","CAP_EDGE",EDGE,{"disambiguationData":[OSD([sQuery(id+"F3.wireOp",EDGE,"E50")])],"isStart":true})});
            var Q12;
            Q12=makeQuery(id+"F4.boolean.opBoolean","COPY",EDGE,{"derivedFrom":makeQuery(id+"F4.opExtrude","CAP_EDGE",EDGE,{"disambiguationData":[OSD([sQuery(id+"F3.wireOp",EDGE,"E13")])],"isStart":true})});
            var Q13;
            Q13=makeQuery(id+"F4.boolean.opBoolean","COPY",EDGE,{"derivedFrom":makeQuery(id+"F4.opExtrude","CAP_EDGE",EDGE,{"disambiguationData":[OSD([sQuery(id+"F3.wireOp",EDGE,"E47.trimOffspring")])],"isStart":true})});
            var Q14;
            Q14=makeQuery(id+"F4.boolean.opBoolean","COPY",EDGE,{"derivedFrom":makeQuery(id+"F4.opExtrude","CAP_EDGE",EDGE,{"disambiguationData":[OSD([sQuery(id+"F3.wireOp",EDGE,"E20")])],"isStart":true})});
            var Q15;
            Q15=makeQuery(id+"F4.boolean.opBoolean","COPY",EDGE,{"derivedFrom":makeQuery(id+"F4.opExtrude","CAP_EDGE",EDGE,{"disambiguationData":[OSD([sQuery(id+"F3.wireOp",EDGE,"E18")])],"isStart":true})});
            var Q16;
            Q16=makeQuery(id+"F4.boolean.opBoolean","COPY",EDGE,{"derivedFrom":makeQuery(id+"F4.opExtrude","CAP_EDGE",EDGE,{"disambiguationData":[OSD([sQuery(id+"F3.wireOp",EDGE,"E17")])],"isStart":true})});
            var Q17;
            Q17=makeQuery(id+"F4.boolean.opBoolean","COPY",EDGE,{"derivedFrom":makeQuery(id+"F4.opExtrude","CAP_EDGE",EDGE,{"disambiguationData":[OSD([sQuery(id+"F3.wireOp",EDGE,"E45")])],"isStart":true})});
            var Q18;
            Q18=makeQuery(id+"F4.boolean.opBoolean","COPY",EDGE,{"derivedFrom":makeQuery(id+"F4.opExtrude","CAP_EDGE",EDGE,{"disambiguationData":[OSD([sQuery(id+"F3.wireOp",EDGE,"E19")])],"isStart":true})});
            var Q19;
            Q19=makeQuery(id+"F4.boolean.opBoolean","COPY",EDGE,{"derivedFrom":makeQuery(id+"F4.opExtrude","CAP_EDGE",EDGE,{"disambiguationData":[OSD([sQuery(id+"F3.wireOp",EDGE,"E22")])],"isStart":true})});
            var Q20;
            Q20=makeQuery(id+"F4.boolean.opBoolean","COPY",EDGE,{"derivedFrom":makeQuery(id+"F4.opExtrude","CAP_EDGE",EDGE,{"disambiguationData":[OSD([sQuery(id+"F3.wireOp",EDGE,"E23")])],"isStart":true})});
            var Q21;
            Q21=makeQuery(id+"F4.boolean.opBoolean","COPY",EDGE,{"derivedFrom":makeQuery(id+"F4.opExtrude","CAP_EDGE",EDGE,{"disambiguationData":[OSD([sQuery(id+"F3.wireOp",EDGE,"E48.trimOffspring")])],"isStart":true})});
            var Q22;
            Q22=makeQuery(id+"F4.boolean.opBoolean","COPY",EDGE,{"derivedFrom":makeQuery(id+"F4.opExtrude","CAP_EDGE",EDGE,{"disambiguationData":[OSD([sQuery(id+"F3.wireOp",EDGE,"E24")])],"isStart":true})});
            var Q23;
            Q23=makeQuery(id+"F4.boolean.opBoolean","COPY",EDGE,{"derivedFrom":makeQuery(id+"F4.opExtrude","CAP_EDGE",EDGE,{"disambiguationData":[OSD([sQuery(id+"F3.wireOp",EDGE,"E27")])],"isStart":true})});
            var Q24;
            Q24=makeQuery(id+"F4.boolean.opBoolean","COPY",EDGE,{"derivedFrom":makeQuery(id+"F4.opExtrude","CAP_EDGE",EDGE,{"disambiguationData":[OSD([sQuery(id+"F3.wireOp",EDGE,"E32.trimOffspring")])],"isStart":true})});
            var Q25;
            Q25=makeQuery(id+"F4.boolean.opBoolean","COPY",EDGE,{"derivedFrom":makeQuery(id+"F4.opExtrude","CAP_EDGE",EDGE,{"disambiguationData":[OSD([sQuery(id+"F3.wireOp",EDGE,"E30.trimOffspring")])],"isStart":true})});
            var Q26;
            Q26=makeQuery(id+"F4.boolean.opBoolean","COPY",EDGE,{"derivedFrom":makeQuery(id+"F4.opExtrude","CAP_EDGE",EDGE,{"disambiguationData":[OSD([sQuery(id+"F3.wireOp",EDGE,"E15")])],"isStart":true})});
            var Q27;
            Q27=makeQuery(id+"F4.boolean.opBoolean","COPY",EDGE,{"derivedFrom":makeQuery(id+"F4.opExtrude","CAP_EDGE",EDGE,{"disambiguationData":[OSD([sQuery(id+"F3.wireOp",EDGE,"E33")])],"isStart":true})});
            var Q28;
            Q28=makeQuery(id+"F4.boolean.opBoolean","COPY",EDGE,{"derivedFrom":makeQuery(id+"F4.opExtrude","CAP_EDGE",EDGE,{"disambiguationData":[OSD([sQuery(id+"F3.wireOp",EDGE,"E14")])],"isStart":true})});
            var Q29;
            Q29=makeQuery(id+"F4.boolean.opBoolean","COPY",EDGE,{"derivedFrom":makeQuery(id+"F4.opExtrude","CAP_EDGE",EDGE,{"disambiguationData":[OSD([sQuery(id+"F3.wireOp",EDGE,"E35")])],"isStart":true})});
            var Q30;
            Q30=makeQuery(id+"F4.boolean.opBoolean","COPY",EDGE,{"derivedFrom":makeQuery(id+"F4.opExtrude","CAP_EDGE",EDGE,{"disambiguationData":[OSD([sQuery(id+"F3.wireOp",EDGE,"E38")])],"isStart":true})});
            var Q31;
            Q31=makeQuery(id+"F4.boolean.opBoolean","COPY",EDGE,{"derivedFrom":makeQuery(id+"F4.opExtrude","CAP_EDGE",EDGE,{"disambiguationData":[OSD([sQuery(id+"F3.wireOp",EDGE,"E29")])],"isStart":true})});
            fillet(context, id + "F6", {"entities" : qUnion([Q0, Q1, Q2, Q3, Q4, Q5, Q6, Q7, Q8, Q9, Q10, Q11, Q12, Q13, Q14, Q15, Q16, Q17, Q18, Q19, Q20, Q21, Q22, Q23, Q24, Q25, Q26, Q27, Q28, Q29, Q30, Q31]), "radius" : 1.02 * mm, "tangentPropagation" : true, "allowEdgeOverflow" : false});
        }
        {
            var Q0;
            Q0=makeQuery(id+"F4.boolean.opBoolean","COPY",EDGE,{"derivedFrom":makeQuery(id+"F4.opExtrude","CAP_EDGE",EDGE,{"disambiguationData":[OSD([sQuery(id+"F3.wireOp",EDGE,"E37")])],"isStart":true})});
            var Q1;
            Q1=makeQuery(id+"F4.boolean.opBoolean","COPY",EDGE,{"derivedFrom":makeQuery(id+"F4.opExtrude","CAP_EDGE",EDGE,{"disambiguationData":[OSD([sQuery(id+"F3.wireOp",EDGE,"E34")])],"isStart":true})});
            var Q2;
            Q2=makeQuery(id+"F4.boolean.opBoolean","COPY",EDGE,{"derivedFrom":makeQuery(id+"F4.opExtrude","CAP_EDGE",EDGE,{"disambiguationData":[OSD([sQuery(id+"F3.wireOp",EDGE,"E46.trimOffspring")])],"isStart":true})});
            fillet(context, id + "F7", {"entities" : qUnion([Q0, Q1, Q2]), "radius" : 1.02 * mm, "tangentPropagation" : true, "allowEdgeOverflow" : false});
        }
        {
            var Q0;
            Q0=makeQuery(id+"F4.boolean.opBoolean","COPY",EDGE,{"derivedFrom":makeQuery(id+"F4.opExtrude","CAP_EDGE",EDGE,{"disambiguationData":[OSD([sQuery(id+"F3.wireOp",EDGE,"E19")])],"isStart":false})});
            var Q1;
            Q1=makeQuery(id+"F4.boolean.opBoolean","COPY",EDGE,{"derivedFrom":makeQuery(id+"F4.opExtrude","CAP_EDGE",EDGE,{"disambiguationData":[OSD([sQuery(id+"F3.wireOp",EDGE,"E48.trimOffspring")])],"isStart":false})});
            var Q2;
            Q2=makeQuery(id+"F4.boolean.opBoolean","COPY",EDGE,{"derivedFrom":makeQuery(id+"F4.opExtrude","CAP_EDGE",EDGE,{"disambiguationData":[OSD([sQuery(id+"F3.wireOp",EDGE,"E22")])],"isStart":false})});
            var Q3;
            Q3=makeQuery(id+"F4.boolean.opBoolean","COPY",EDGE,{"derivedFrom":makeQuery(id+"F4.opExtrude","CAP_EDGE",EDGE,{"disambiguationData":[OSD([sQuery(id+"F3.wireOp",EDGE,"E20")])],"isStart":false})});
            var Q4;
            Q4=makeQuery(id+"F4.boolean.opBoolean","COPY",EDGE,{"derivedFrom":makeQuery(id+"F4.opExtrude","CAP_EDGE",EDGE,{"disambiguationData":[OSD([sQuery(id+"F3.wireOp",EDGE,"E13")])],"isStart":false})});
            var Q5;
            Q5=makeQuery(id+"F4.boolean.opBoolean","COPY",EDGE,{"derivedFrom":makeQuery(id+"F4.opExtrude","CAP_EDGE",EDGE,{"disambiguationData":[OSD([sQuery(id+"F3.wireOp",EDGE,"E45")])],"isStart":false})});
            var Q6;
            Q6=makeQuery(id+"F4.boolean.opBoolean","COPY",EDGE,{"derivedFrom":makeQuery(id+"F4.opExtrude","CAP_EDGE",EDGE,{"disambiguationData":[OSD([sQuery(id+"F3.wireOp",EDGE,"E17")])],"isStart":false})});
            fillet(context, id + "F8", {"entities" : qUnion([Q0, Q1, Q2, Q3, Q4, Q5, Q6]), "radius" : 1.02 * mm, "tangentPropagation" : true, "allowEdgeOverflow" : false});
        }
        {
            var Q0;
            Q0=makeQuery(id+"F4.boolean.opBoolean","COPY",EDGE,{"derivedFrom":makeQuery(id+"F4.opExtrude","CAP_EDGE",EDGE,{"disambiguationData":[OSD([sQuery(id+"F3.wireOp",EDGE,"E29")])],"isStart":false})});
            var Q1;
            Q1=makeQuery(id+"F4.boolean.opBoolean","COPY",EDGE,{"derivedFrom":makeQuery(id+"F4.opExtrude","CAP_EDGE",EDGE,{"disambiguationData":[OSD([sQuery(id+"F3.wireOp",EDGE,"E38")])],"isStart":false})});
            var Q2;
            Q2=makeQuery(id+"F4.boolean.opBoolean","COPY",EDGE,{"derivedFrom":makeQuery(id+"F4.opExtrude","CAP_EDGE",EDGE,{"disambiguationData":[OSD([sQuery(id+"F3.wireOp",EDGE,"E16")])],"isStart":false})});
            var Q3;
            Q3=makeQuery(id+"F4.boolean.opBoolean","COPY",EDGE,{"derivedFrom":makeQuery(id+"F4.opExtrude","SWEPT_EDGE",EDGE,{"disambiguationData":[OSD([sQuery(id+"F3.wireOp",EDGE,"E23"),sQuery(id+"F3.wireOp",EDGE,"E24")])]})});
            var Q4;
            Q4=makeQuery(id+"F4.boolean.opBoolean","COPY",EDGE,{"derivedFrom":makeQuery(id+"F4.opExtrude","CAP_EDGE",EDGE,{"disambiguationData":[OSD([sQuery(id+"F3.wireOp",EDGE,"E23")])],"isStart":false})});
            fillet(context, id + "F9", {"entities" : qUnion([Q0, Q1, Q2, Q3, Q4]), "radius" : 1.02 * mm, "tangentPropagation" : true, "allowEdgeOverflow" : false});
        }
        {
            var Q0;
            Q0=makeQuery(id+"F6.opFillet","BLEND_EDGE",EDGE,{"blendedFrom":[makeQuery(id+"F4.boolean.opBoolean","COPY",EDGE,{"derivedFrom":makeQuery(id+"F4.opExtrude","CAP_EDGE",EDGE,{"disambiguationData":[OSD([sQuery(id+"F3.wireOp",EDGE,"E25")])],"isStart":true})}),makeQuery(id+"F4.boolean.opBoolean","COPY",FACE,{"derivedFrom":makeQuery(id+"F4.opExtrude","SWEPT_FACE",FACE,{"disambiguationData":[OSD([sQuery(id+"F3.wireOp",EDGE,"E44")])]})})],"blendedInto":[makeQuery(id+"F4.boolean.opBoolean","COPY",FACE,{"derivedFrom":makeQuery(id+"F4.opExtrude","SWEPT_FACE",FACE,{"disambiguationData":[OSD([sQuery(id+"F3.wireOp",EDGE,"E44")])]})})]});
            var Q1;
            Q1=makeQuery(id+"F4.boolean.opBoolean","COPY",EDGE,{"derivedFrom":makeQuery(id+"F4.opExtrude","SWEPT_EDGE",EDGE,{"disambiguationData":[OSD([sQuery(id+"F3.wireOp",EDGE,"E32.trimOffspring"),sQuery(id+"F3.wireOp",EDGE,"E44")])]})});
            fillet(context, id + "F10", {"entities" : qUnion([Q0, Q1]), "radius" : 1.02 * mm, "tangentPropagation" : true, "allowEdgeOverflow" : false});
        }
        {
            var Q0;
            Q0=makeQuery(id+"F4.boolean.opBoolean","COPY",EDGE,{"derivedFrom":makeQuery(id+"F4.opExtrude","CAP_EDGE",EDGE,{"disambiguationData":[OSD([sQuery(id+"F3.wireOp",EDGE,"E18")])],"isStart":false})});
            var Q1;
            Q1=makeQuery(id+"F4.boolean.opBoolean","COPY",EDGE,{"derivedFrom":makeQuery(id+"F4.opExtrude","CAP_EDGE",EDGE,{"disambiguationData":[OSD([sQuery(id+"F3.wireOp",EDGE,"E39")])],"isStart":false})});
            fillet(context, id + "F11", {"entities" : qUnion([Q0, Q1]), "radius" : 1.02 * mm, "tangentPropagation" : true, "allowEdgeOverflow" : false});
        }
        {
            var Q0;
            Q0=makeQuery(id+"F4.boolean.opBoolean","COPY",EDGE,{"derivedFrom":makeQuery(id+"F4.opExtrude","CAP_EDGE",EDGE,{"disambiguationData":[OSD([sQuery(id+"F3.wireOp",EDGE,"E47.trimOffspring")])],"isStart":false})});
            var Q1;
            Q1=makeQuery(id+"F4.boolean.opBoolean","COPY",EDGE,{"derivedFrom":makeQuery(id+"F4.opExtrude","CAP_EDGE",EDGE,{"disambiguationData":[OSD([sQuery(id+"F3.wireOp",EDGE,"E33")])],"isStart":false})});
            fillet(context, id + "F12", {"entities" : qUnion([Q0, Q1]), "radius" : 1.02 * mm, "tangentPropagation" : true, "allowEdgeOverflow" : false});
        }
        {
            var Q0;
            Q0=makeQuery(id+"F4.boolean.opBoolean","COPY",EDGE,{"derivedFrom":makeQuery(id+"F4.opExtrude","CAP_EDGE",EDGE,{"disambiguationData":[OSD([sQuery(id+"F3.wireOp",EDGE,"E14")])],"isStart":false})});
            var Q1;
            Q1=makeQuery(id+"F4.boolean.opBoolean","COPY",EDGE,{"derivedFrom":makeQuery(id+"F4.opExtrude","CAP_EDGE",EDGE,{"disambiguationData":[OSD([sQuery(id+"F3.wireOp",EDGE,"E15")])],"isStart":false})});
            fillet(context, id + "F13", {"entities" : qUnion([Q0, Q1]), "radius" : 1.02 * mm, "tangentPropagation" : true, "allowEdgeOverflow" : false});
        }
        {
            var Q0;
            Q0=makeQuery(id+"F9.opFillet","BLEND_EDGE",EDGE,{"blendedFrom":[makeQuery(id+"F4.boolean.opBoolean","COPY",EDGE,{"derivedFrom":makeQuery(id+"F4.opExtrude","CAP_EDGE",EDGE,{"disambiguationData":[OSD([sQuery(id+"F3.wireOp",EDGE,"E24")])],"isStart":false})}),makeQuery(id+"F8.opFillet","BLEND_FACE",FACE,{"disambiguationData":[OSD([sQuery(id+"F3.wireOp",EDGE,"E48.trimOffspring")])]})],"blendedInto":[makeQuery(id+"F8.opFillet","BLEND_FACE",FACE,{"disambiguationData":[OSD([sQuery(id+"F3.wireOp",EDGE,"E48.trimOffspring")])]})]});
            var Q1;
            Q1=makeQuery(id+"F11.opFillet","BLEND_EDGE",EDGE,{"blendedFrom":[makeQuery(id+"F4.boolean.opBoolean","COPY",EDGE,{"derivedFrom":makeQuery(id+"F4.opExtrude","CAP_EDGE",EDGE,{"disambiguationData":[OSD([sQuery(id+"F3.wireOp",EDGE,"E39")])],"isStart":false})}),makeQuery(id+"F9.opFillet","BLEND_FACE",FACE,{"disambiguationData":[OSD([sQuery(id+"F3.wireOp",EDGE,"E38")])]})],"blendedInto":[makeQuery(id+"F9.opFillet","BLEND_FACE",FACE,{"disambiguationData":[OSD([sQuery(id+"F3.wireOp",EDGE,"E38")])]})]});
            var Q2;
            Q2=makeQuery(id+"F9.opFillet","BLEND_EDGE",EDGE,{"blendedFrom":[makeQuery(id+"F4.boolean.opBoolean","COPY",EDGE,{"derivedFrom":makeQuery(id+"F4.opExtrude","CAP_EDGE",EDGE,{"disambiguationData":[OSD([sQuery(id+"F3.wireOp",EDGE,"E29")])],"isStart":false})}),makeQuery(id+"F8.opFillet","BLEND_FACE",FACE,{"disambiguationData":[OSD([sQuery(id+"F3.wireOp",EDGE,"E45")])]})],"blendedInto":[makeQuery(id+"F8.opFillet","BLEND_FACE",FACE,{"disambiguationData":[OSD([sQuery(id+"F3.wireOp",EDGE,"E45")])]})]});
            var Q3;
            Q3=makeQuery(id+"F11.opFillet","BLEND_EDGE",EDGE,{"blendedFrom":[makeQuery(id+"F4.boolean.opBoolean","COPY",EDGE,{"derivedFrom":makeQuery(id+"F4.opExtrude","CAP_EDGE",EDGE,{"disambiguationData":[OSD([sQuery(id+"F3.wireOp",EDGE,"E18")])],"isStart":false})}),makeQuery(id+"F8.opFillet","BLEND_FACE",FACE,{"disambiguationData":[OSD([sQuery(id+"F3.wireOp",EDGE,"E17")])]})],"blendedInto":[makeQuery(id+"F8.opFillet","BLEND_FACE",FACE,{"disambiguationData":[OSD([sQuery(id+"F3.wireOp",EDGE,"E17")])]})]});
            var Q4;
            Q4=makeQuery(id+"F8.opFillet","BLEND_EDGE",EDGE,{"blendedFrom":[makeQuery(id+"F4.boolean.opBoolean","COPY",EDGE,{"derivedFrom":makeQuery(id+"F4.opExtrude","CAP_EDGE",EDGE,{"disambiguationData":[OSD([sQuery(id+"F3.wireOp",EDGE,"E19")])],"isStart":false})}),makeQuery(id+"F4.boolean.opBoolean","COPY",EDGE,{"derivedFrom":makeQuery(id+"F4.opExtrude","CAP_EDGE",EDGE,{"disambiguationData":[OSD([sQuery(id+"F3.wireOp",EDGE,"E48.trimOffspring")])],"isStart":false})})],"blendedInto":[]});
            var Q5;
            Q5=makeQuery(id+"F8.opFillet","BLEND_EDGE",EDGE,{"blendedFrom":[makeQuery(id+"F4.boolean.opBoolean","COPY",EDGE,{"derivedFrom":makeQuery(id+"F4.opExtrude","CAP_EDGE",EDGE,{"disambiguationData":[OSD([sQuery(id+"F3.wireOp",EDGE,"E19")])],"isStart":false})}),makeQuery(id+"F4.boolean.opBoolean","COPY",EDGE,{"derivedFrom":makeQuery(id+"F4.opExtrude","CAP_EDGE",EDGE,{"disambiguationData":[OSD([sQuery(id+"F3.wireOp",EDGE,"E22")])],"isStart":false})})],"blendedInto":[]});
            var Q6;
            Q6=makeQuery(id+"F9.opFillet","BLEND_EDGE",EDGE,{"blendedFrom":[makeQuery(id+"F4.boolean.opBoolean","COPY",EDGE,{"derivedFrom":makeQuery(id+"F4.opExtrude","CAP_EDGE",EDGE,{"disambiguationData":[OSD([sQuery(id+"F3.wireOp",EDGE,"E23")])],"isStart":false})}),makeQuery(id+"F8.opFillet","BLEND_FACE",FACE,{"disambiguationData":[OSD([sQuery(id+"F3.wireOp",EDGE,"E22")])]})],"blendedInto":[makeQuery(id+"F8.opFillet","BLEND_FACE",FACE,{"disambiguationData":[OSD([sQuery(id+"F3.wireOp",EDGE,"E22")])]})]});
            fillet(context, id + "F14", {"entities" : qUnion([Q0, Q1, Q2, Q3, Q4, Q5, Q6]), "radius" : 1.02 * mm, "tangentPropagation" : true, "allowEdgeOverflow" : false});
        }
    });
